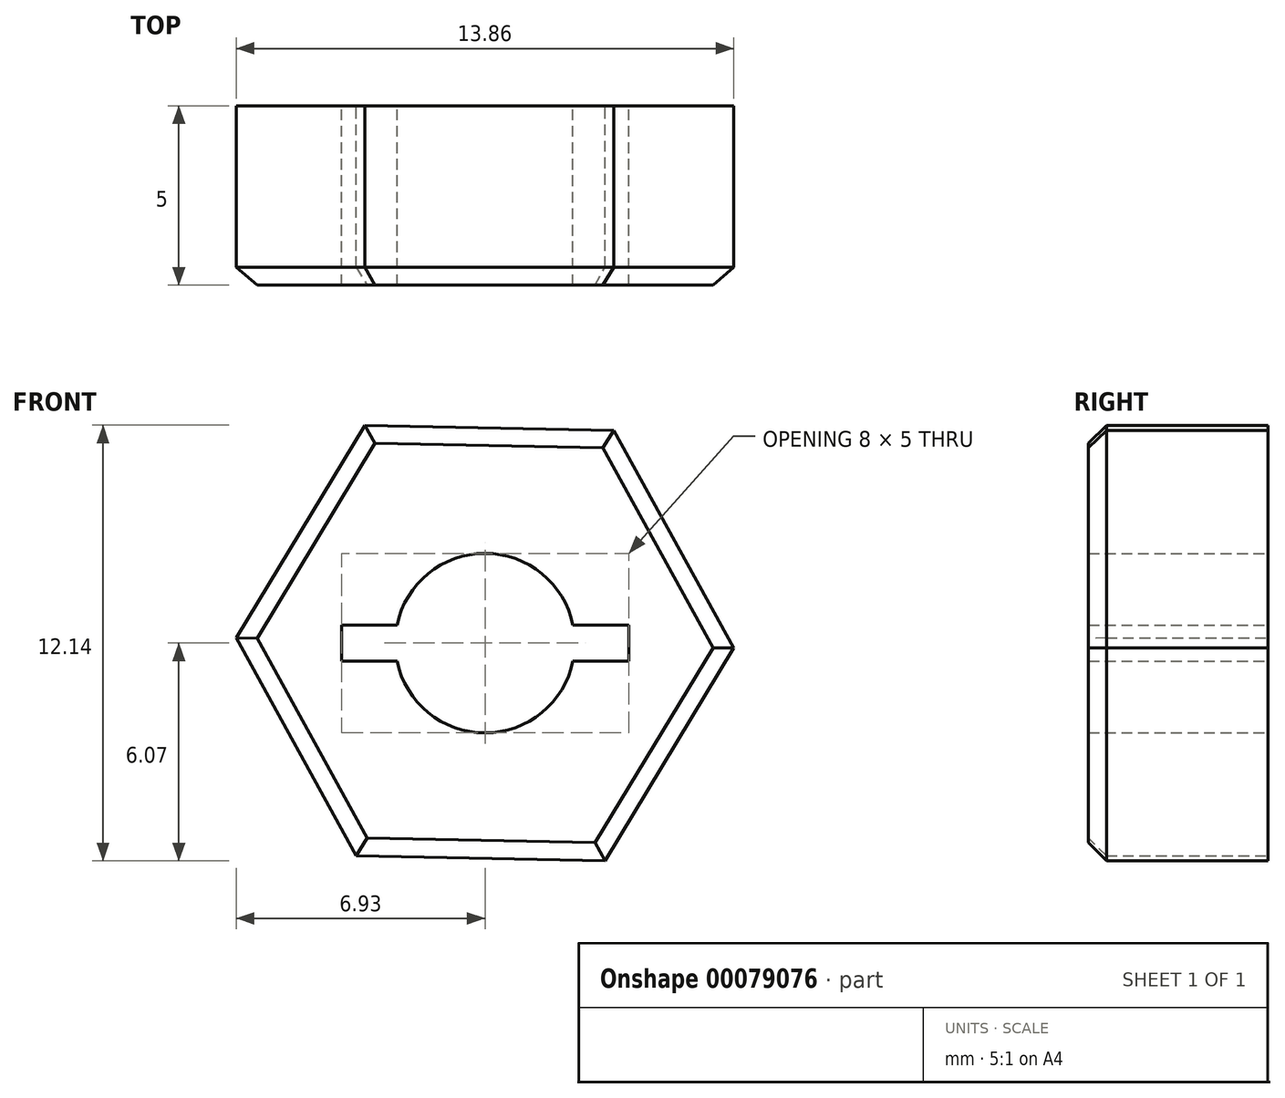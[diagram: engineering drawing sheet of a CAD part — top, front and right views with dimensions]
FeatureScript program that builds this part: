
annotation { "Feature Type Name" : "Feature", "Feature Type Description" : "" }
export const myFeature = defineFeature(function(context is Context, id is Id, definition is map)
    precondition{}
    {
        {
            var Q0;
            Q0=qCreatedBy(makeId("Front.planeOp"),FACE);
            var sketch = newSketch(context, id + "F5", { "sketchPlane" : qUnion([Q0])});
            skCircle(sketch, "E0.cCircle", {"center": v(0, 0) * mm, "radius": 6 * mm, "construction": true});
            skLineSegment(sketch, "E0.0", {"start": v(3.58, 5.93) * mm, "end": v(6.93, -0.14) * mm});
            skLineSegment(sketch, "E0.1", {"start": v(6.93, -0.14) * mm, "end": v(3.34, -6.07) * mm});
            skLineSegment(sketch, "E0.2", {"start": v(3.34, -6.07) * mm, "end": v(-3.58, -5.93) * mm});
            skLineSegment(sketch, "E0.3", {"start": v(-3.58, -5.93) * mm, "end": v(-6.93, 0.14) * mm});
            skLineSegment(sketch, "E0.4", {"start": v(-6.93, 0.14) * mm, "end": v(-3.34, 6.07) * mm});
            skLineSegment(sketch, "E0.5", {"start": v(-3.34, 6.07) * mm, "end": v(3.58, 5.93) * mm});
            skPoint(sketch, "E0.0.midPoint", {"position": v(5.26, 2.9) * mm});
            skSolve(sketch);
        }
        {
            var Q0;
            Q0=makeQuery(id+"F5.imprint","IMPRINT",FACE,{"disambiguationData":[TD([[makeQuery(id+"F5.imprint","IMPRINT",EDGE,{"derivedFrom":sQuery(id+"F5.wireOp",EDGE,"E0.0")}),-1.0]])]});
            extrude(context, id + "F0", {"entities" : qUnion([Q0]), "depth" : 5 * mm});
        }
        {
            var Q0;
            Q0=makeQuery(id+"F5.imprint","IMPRINT",FACE,{"disambiguationData":[TD([[makeQuery(id+"F5.imprint","IMPRINT",EDGE,{"derivedFrom":sQuery(id+"F5.wireOp",EDGE,"E0.0")}),-1.0]])]});
            var sketch = newSketch(context, id + "F1", { "sketchPlane" : qUnion([Q0])});
            skCircle(sketch, "E1", {"center": v(0, 0) * mm, "radius": 2.5 * mm});
            skSolve(sketch);
        }
        {
            var Q0;
            Q0=makeQuery(id+"F1.imprint","IMPRINT",FACE,{"disambiguationData":[TD([[makeQuery(id+"F1.imprint","IMPRINT",EDGE,{"derivedFrom":sQuery(id+"F1.wireOp",EDGE,"E1")}),1.0]])]});
            extrude(context, id + "F2", {"entities" : qUnion([Q0]), "operationType" : NewBodyOperationType.REMOVE, "depth" : 36.5 * mm});
        }
        {
            var Q0;
            Q0=makeQuery(id+"F0.opExtrude","CAP_EDGE",EDGE,{"disambiguationData":[OSD([sQuery(id+"F5.wireOp",EDGE,"E0.3")])],"isStart":false});
            var Q1;
            Q1=makeQuery(id+"F0.opExtrude","CAP_EDGE",EDGE,{"disambiguationData":[OSD([sQuery(id+"F5.wireOp",EDGE,"E0.4")])],"isStart":false});
            var Q2;
            Q2=makeQuery(id+"F0.opExtrude","CAP_EDGE",EDGE,{"disambiguationData":[OSD([sQuery(id+"F5.wireOp",EDGE,"E0.5")])],"isStart":false});
            var Q3;
            Q3=makeQuery(id+"F0.opExtrude","CAP_EDGE",EDGE,{"disambiguationData":[OSD([sQuery(id+"F5.wireOp",EDGE,"E0.0")])],"isStart":false});
            var Q4;
            Q4=makeQuery(id+"F0.opExtrude","CAP_EDGE",EDGE,{"disambiguationData":[OSD([sQuery(id+"F5.wireOp",EDGE,"E0.2")])],"isStart":false});
            var Q5;
            Q5=makeQuery(id+"F0.opExtrude","CAP_EDGE",EDGE,{"disambiguationData":[OSD([sQuery(id+"F5.wireOp",EDGE,"E0.1")])],"isStart":false});
            chamfer(context, id + "F6", {"entities" : qUnion([Q0, Q1, Q2, Q3, Q4, Q5]), "width" : 0.5 * mm, "tangentPropagation" : true});
        }
        {
            var Q0;
            Q0=makeQuery(id+"F5.imprint","IMPRINT",FACE,{"disambiguationData":[TD([[makeQuery(id+"F5.imprint","IMPRINT",EDGE,{"derivedFrom":sQuery(id+"F5.wireOp",EDGE,"E0.0")}),-1.0]])]});
            var sketch = newSketch(context, id + "F3", { "sketchPlane" : qUnion([Q0])});
            skLineSegment(sketch, "E2.bottom", {"start": v(-4, 0.5) * mm, "end": v(4, 0.5) * mm});
            skLineSegment(sketch, "E2.top", {"start": v(-4, -0.5) * mm, "end": v(4, -0.5) * mm});
            skLineSegment(sketch, "E2.left", {"start": v(-4, 0.5) * mm, "end": v(-4, -0.5) * mm});
            skLineSegment(sketch, "E2.right", {"start": v(4, 0.5) * mm, "end": v(4, -0.5) * mm});
            skPoint(sketch, "E2.middle", {"position": v(0, 0) * mm});
            skSolve(sketch);
        }
        {
            var Q0;
            Q0 = qSketchRegion(id + "F3", true);
            extrude(context, id + "F4", {"entities" : qUnion([Q0]), "operationType" : NewBodyOperationType.REMOVE, "depth" : 5.53 * mm});
        }
    });
